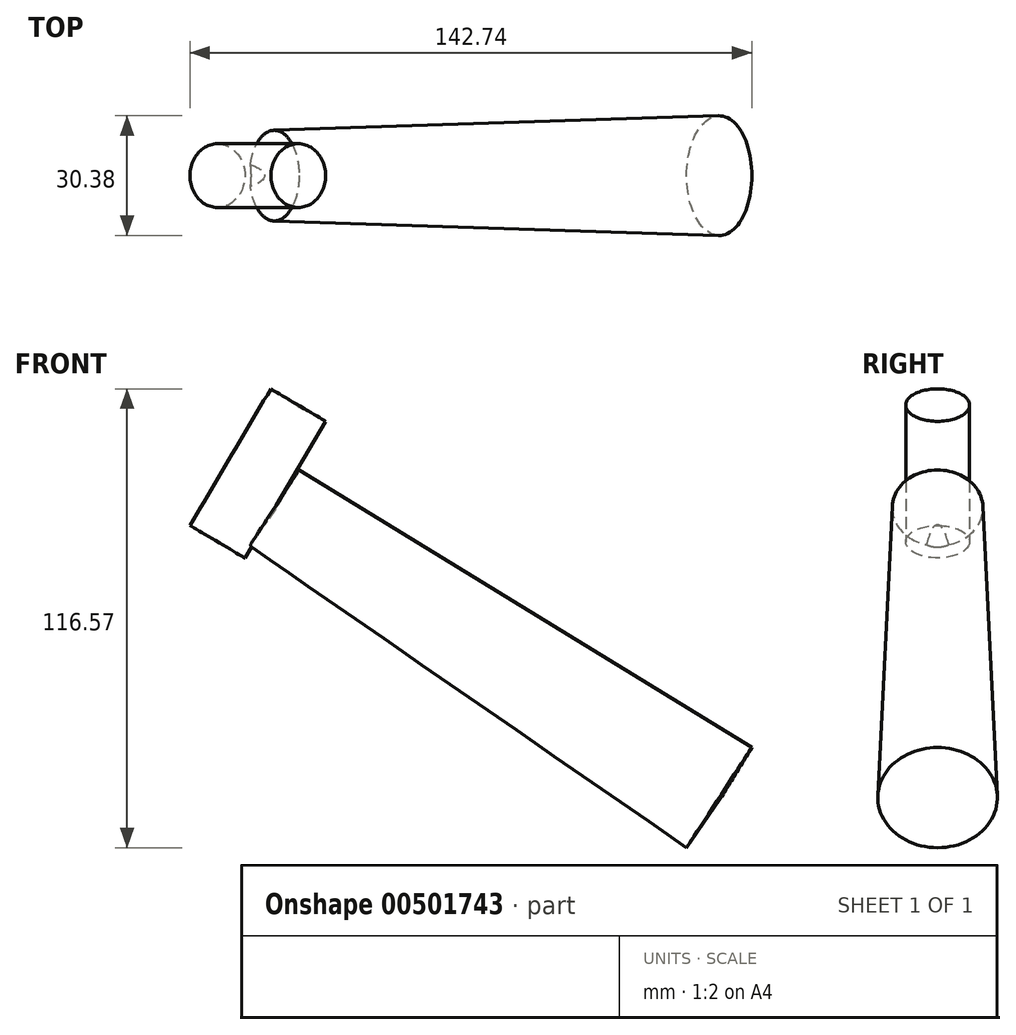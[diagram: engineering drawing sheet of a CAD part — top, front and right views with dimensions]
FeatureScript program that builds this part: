
annotation { "Feature Type Name" : "Feature", "Feature Type Description" : "" }
export const myFeature = defineFeature(function(context is Context, id is Id, definition is map)
    precondition{}
    {
        {
            var Q0;
            Q0=qCreatedBy(makeId("Front.planeOp"),FACE);
            var sketch = newSketch(context, id + "F0", { "sketchPlane" : qUnion([Q0])});
            skLineSegment(sketch, "E0", {"start": v(-28.01, 43.27) * mm, "end": v(-48.54, 8.55) * mm});
            skLineSegment(sketch, "E1", {"start": v(-48.54, 8.55) * mm, "end": v(-55.51, 12.67) * mm});
            skLineSegment(sketch, "E2", {"start": v(-55.51, 12.67) * mm, "end": v(-35.15, 47.12) * mm});
            skLineSegment(sketch, "E3", {"start": v(-35.15, 47.12) * mm, "end": v(-28.01, 43.27) * mm});
            skSolve(sketch);
        }
        {
            var Q0;
            Q0 = qSketchRegion(id + "F0", true);
            var Q1;
            Q1=sQuery(id+"F0.wireOp",EDGE,"E2");
            revolve(context, id + "F1", {"entities" : qUnion([Q0]), "axis" : qUnion([Q1]), "revolveType" : RevolveType.FULL});
        }
        {
            var Q0;
            Q0=qCreatedBy(makeId("Front.planeOp"),FACE);
            var sketch = newSketch(context, id + "F2", { "sketchPlane" : qUnion([Q0])});
            skLineSegment(sketch, "E4", {"start": v(-47.34, 11.63) * mm, "end": v(63.68, -65.06) * mm});
            skLineSegment(sketch, "E5", {"start": v(63.68, -65.06) * mm, "end": v(72.31, -52.55) * mm});
            skLineSegment(sketch, "E6", {"start": v(72.31, -52.55) * mm, "end": v(-40.7, 21.04) * mm});
            skLineSegment(sketch, "E7", {"start": v(-40.7, 21.04) * mm, "end": v(-47.34, 11.63) * mm});
            skSolve(sketch);
        }
        {
            var Q0;
            Q0=makeQuery(id+"F2.imprint","IMPRINT",FACE,{"disambiguationData":[TD([[makeQuery(id+"F2.imprint","IMPRINT",EDGE,{"derivedFrom":sQuery(id+"F2.wireOp",EDGE,"E4")}),1.0]])]});
            var Q1;
            Q1=sQuery(id+"F2.wireOp",EDGE,"E6");
            revolve(context, id + "F3", {"operationType" : NewBodyOperationType.ADD, "entities" : qUnion([Q0]), "axis" : qUnion([Q1]), "revolveType" : RevolveType.FULL});
        }
    });
